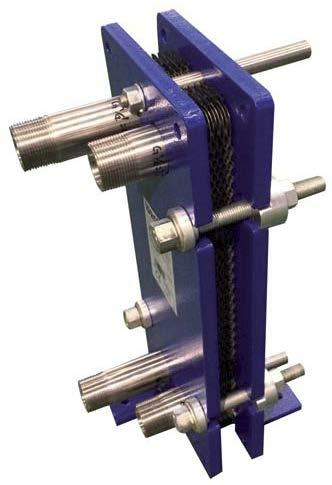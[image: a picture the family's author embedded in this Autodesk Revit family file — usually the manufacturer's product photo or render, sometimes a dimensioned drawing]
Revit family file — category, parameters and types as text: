
# Revit family: IDJ3-12_CC08101
name_source: partatom
category: Aparatos eléctricos
revit_build: Autodesk Revit 2016 (Build: 20150220_1215(x64)
units: mm (PartAtom-declared; Revit-internal decimal feet)

## family parameters
Compartido = No
Corte con vacíos al cargar = No
Cota de conector redondo = Diámetro de uso
Mantener orientación de anotación = No
Número OmniClass = 23.80.00.00
Punto de cálculo de habitación = No
Se basa en plano de trabajo = No
Siempre vertical = Sí
Tipo de pieza = Caja de conexiones
Título OmniClass = Electric Power and Lighting

## types (1)
- IDJ3-12
    Bastidor frontal = Acero templado, pintado epoxi
    Caudal máx. = 1500 l/h
    Conexiones = 316L acero inox.
    Costo = 0 $
    Código de montaje = CC08101
    Descripción = INTERCAMBIADOR PLACAS DESMONTABLE
    Dimensiones máx. = 620x480x180mm
    Fabricante = SALVADOR ESCODA
    Imagen de tipo = IDJ3.jpg
    Juntas = Nitrilo
    Modelo = IDJ3-12 PLACAS
    Placas = 316L acero inox.
    Potencia = 29000Kcal/h
    Presión máx. trabajo = 10 bar
    Temperatura máx. trabajo = 100 ºC
    URL = www.salvadorescoda.com
